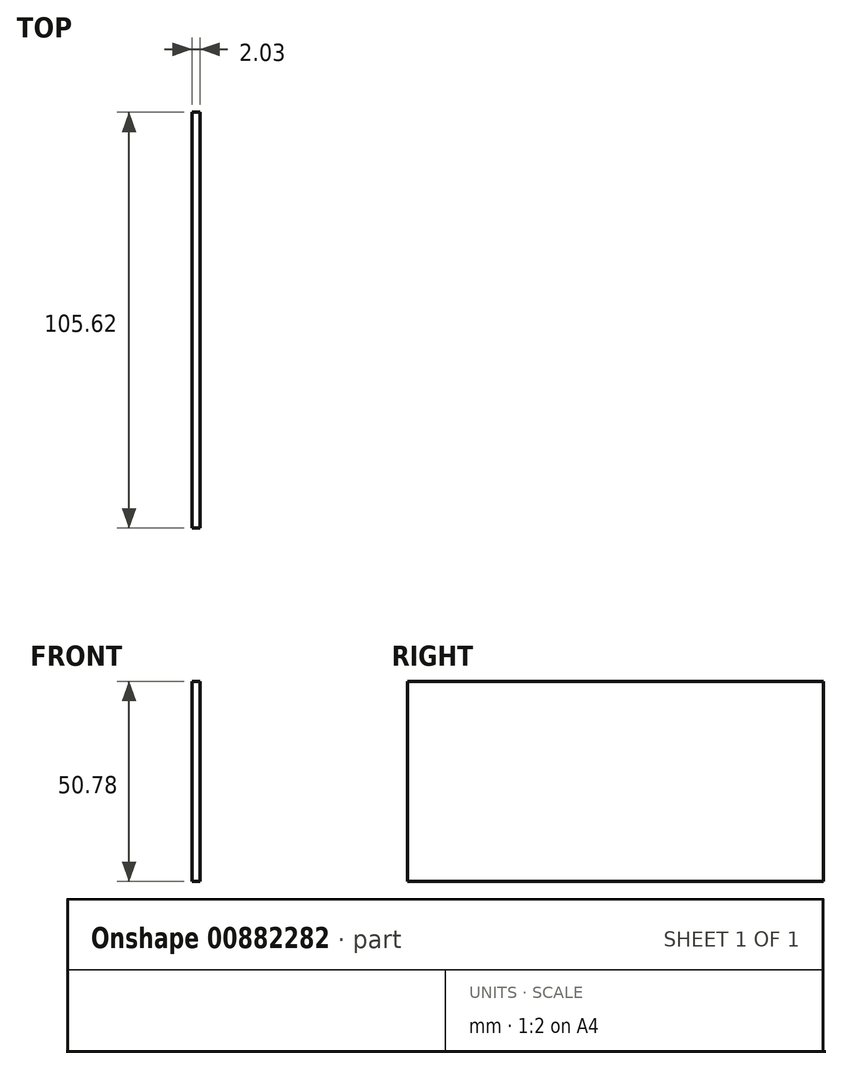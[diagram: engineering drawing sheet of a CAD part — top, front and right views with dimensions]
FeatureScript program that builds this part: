
annotation { "Feature Type Name" : "Feature", "Feature Type Description" : "" }
export const myFeature = defineFeature(function(context is Context, id is Id, definition is map)
    precondition{}
    {
        {
            var Q0;
            Q0=qCreatedBy(makeId("Right.planeOp"),FACE);
            var sketch = newSketch(context, id + "F0", { "sketchPlane" : qUnion([Q0])});
            skLineSegment(sketch, "E0.bottom", {"start": v(52.8, 25.39) * mm, "end": v(-52.8, 25.39) * mm});
            skLineSegment(sketch, "E0.top", {"start": v(52.8, -25.39) * mm, "end": v(-52.8, -25.39) * mm});
            skLineSegment(sketch, "E0.left", {"start": v(52.8, 25.39) * mm, "end": v(52.8, -25.39) * mm});
            skLineSegment(sketch, "E0.right", {"start": v(-52.8, 25.39) * mm, "end": v(-52.8, -25.39) * mm});
            skPoint(sketch, "E0.middle", {"position": v(0, 0) * mm});
            skSolve(sketch);
        }
        {
            var Q0;
            Q0=makeQuery(id+"F0.imprint","IMPRINT",FACE,{"disambiguationData":[TD([[makeQuery(id+"F0.imprint","IMPRINT",EDGE,{"derivedFrom":sQuery(id+"F0.wireOp",EDGE,"E0.bottom")}),1.0]])]});
            extrude(context, id + "F1", {"entities" : qUnion([Q0]), "depth" : 2.03 * mm, "offsetDistance" : 25.4 * mm});
        }
    });
